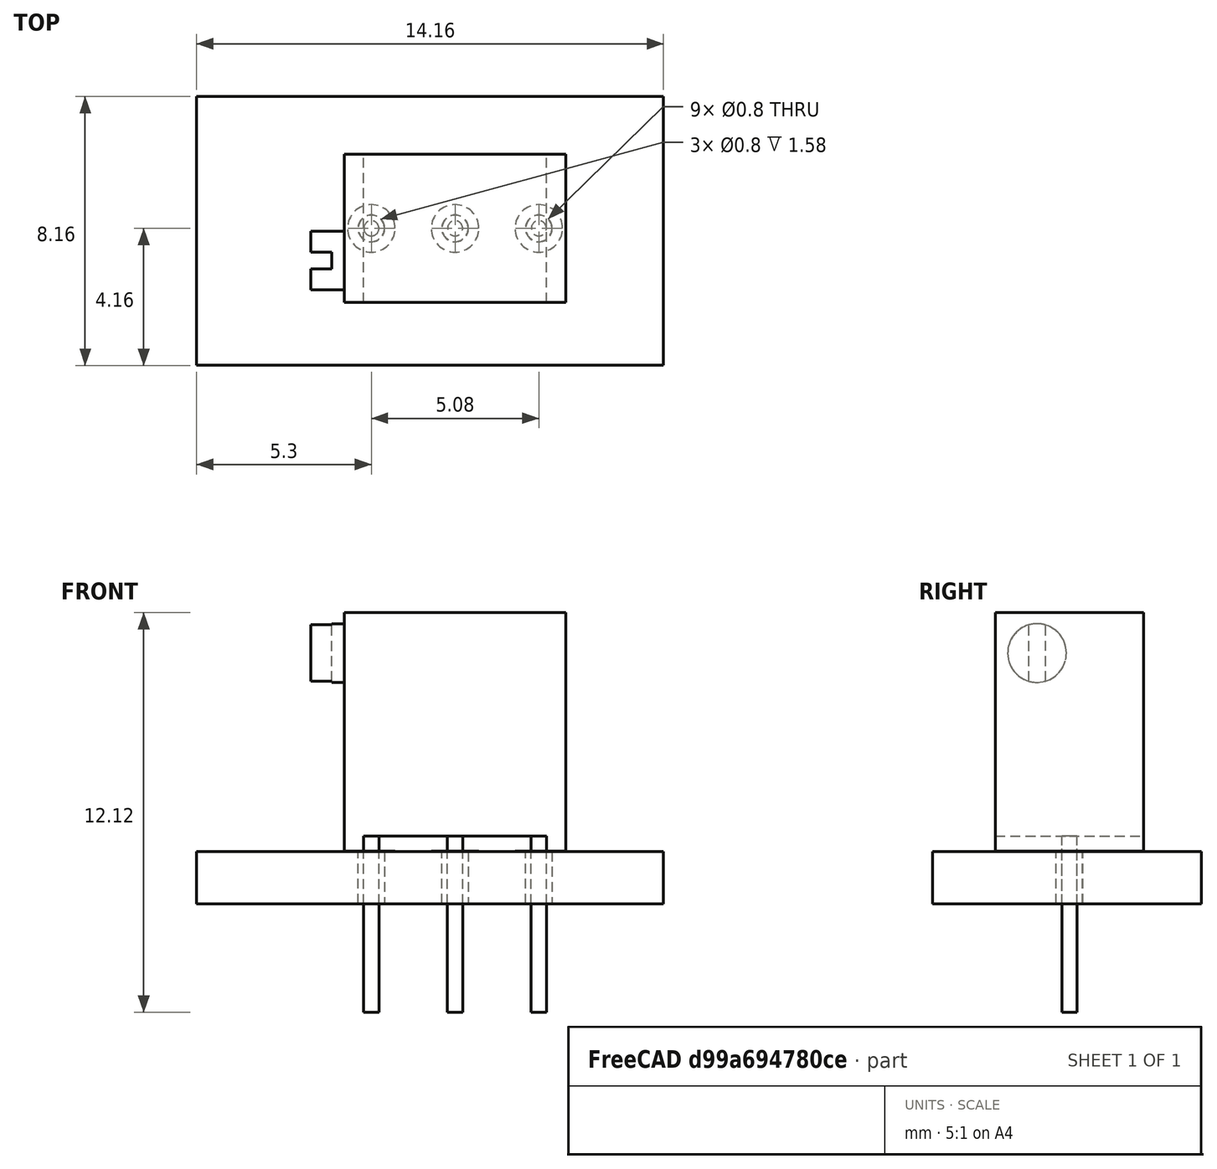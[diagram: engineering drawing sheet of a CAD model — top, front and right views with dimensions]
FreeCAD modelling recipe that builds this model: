
FCSTD DOCUMENT  (FreeCAD 0.18R15611 (Git))
Label: Potentiometer_Bourns_3266Z_Horizontal
License: All rights reserved
LicenseURL: http://en.wikipedia.org/wiki/All_rights_reserved
objects: Part::FeaturePython×7, Part::Cylinder×4, Part::Box×4, Part::MultiFuse×2, App::DocumentObjectGroup×1, Part::Cut×1, Part::Feature×1
note: 19 computed .brp shape members not serialized (recipe doc carries the construction recipe); baked Part::Feature solids carry a one-line shape summary decoded from their .brp

FEATURE [Part::FeaturePython] FCrtYd_lines  label="FCrtYd"  # a2plus imported part (geometry in sourceFile) (typed FeaturePython)
  fixedPosition = true
FEATURE [Part::FeaturePython] FFab_lines  label="FFab"  # a2plus imported part (geometry in sourceFile) (typed FeaturePython)
  fixedPosition = true
FEATURE [Part::FeaturePython] Filk_lines  label="FrontSilk"  # a2plus imported part (geometry in sourceFile) (typed FeaturePython)
  fixedPosition = true
FEATURE [Part::FeaturePython] TopPads  # a2plus imported part (geometry in sourceFile) (typed FeaturePython)
  fixedPosition = true
FEATURE [Part::FeaturePython] BotPads  # a2plus imported part (geometry in sourceFile) (typed FeaturePython)
  fixedPosition = true
FEATURE [Part::FeaturePython] THPs  label="PTHs"  # a2plus imported part (geometry in sourceFile) (typed FeaturePython)
  fixedPosition = true
FEATURE [Part::FeaturePython] newPCB  label="Pcb"  # a2plus imported part (geometry in sourceFile) (typed FeaturePython)
  fixedPosition = true
FEATURE [App::DocumentObjectGroup] Potentiometer_Bourns_3266Z_Horizontal_fp
  Group = -> [FCrtYd_lines,FFab_lines,Filk_lines,TopPads,BotPads,THPs,newPCB]
FEATURE [Part::Cylinder] Cylinder003  label="Knob"
  Angle = 360
  AttacherType = Attacher::AttachEngine3D
  Height = 1.02
  Placement = pos=(-0.405,-2.25,7.24) rot=(0,0,1;0rad)
  Radius = 0.89
FEATURE [Part::Cylinder] Cylinder001  label="Pin3"
  Angle = 360
  AttacherType = Attacher::AttachEngine3D
  Height = 5.34
  Placement = pos=(-5.08,0,-4.88) rot=(0,0,1;0rad)
  Radius = 0.23
FEATURE [Part::Box] Box003  label="Cube"
  AttacherType = Attacher::AttachEngine3D
  Height = 0.64
  Length = 10
  Placement = pos=(-5,-2.5,7.62) rot=(0,0,1;0rad)
  Width = 0.51
FEATURE [Part::Cylinder] Cylinder002  label="Pin2"
  Angle = 360
  AttacherType = Attacher::AttachEngine3D
  Height = 5.34
  Placement = pos=(-2.54,0,-4.88) rot=(0,0,1;0rad)
  Radius = 0.23
FEATURE [Part::Cylinder] Cylinder  label="Pin1"
  Angle = 360
  AttacherType = Attacher::AttachEngine3D
  Height = 5.34
  Placement = pos=(0,0,-4.88) rot=(0,0,1;0rad)
  Radius = 0.23
FEATURE [Part::Box] Box  label="Body"
  AttacherType = Attacher::AttachEngine3D
  Height = 6.78
  Length = 6.71
  Placement = pos=(-5.895,-3.52,0.46) rot=(0,0,1;0rad)
  Width = 4.5
FEATURE [Part::Box] Box001  label="Standoff1"
  AttacherType = Attacher::AttachEngine3D
  Height = 0.46
  Length = 0.585
  Placement = pos=(0.23,-3.52,0) rot=(0,0,1;0rad)
  Width = 4.5
FEATURE [Part::Box] Box002  label="Standoff2"
  AttacherType = Attacher::AttachEngine3D
  Height = 0.46
  Length = 0.585
  Placement = pos=(-5.895,-3.52,0) rot=(0,0,1;0rad)
  Width = 4.5
FEATURE [Part::MultiFuse] Fusion  label="FusionBody"
  Placement = pos=(0,1.27,0) rot=(0,0,1;0rad)
  Refine = true
  Shapes = -> [Box,Box001,Box002]
FEATURE [Part::Cut] Cut  label="CutKnob"
  Base = -> Cylinder003
  Placement = pos=(1.345,1.27,6.42) rot=(0,-1,0;1.5708rad)
  Refine = true
  Tool = -> Box003
FEATURE [Part::MultiFuse] Pin3_mp_cp  label="Pin3_fd"
  Refine = true
  Shapes = -> [Cylinder001,Cylinder002,Cylinder,Fusion,Cut]
FEATURE [Part::Feature] Shape  label="Potentiometer_Bourns_3266Z_Horizontal"
  shape: bbox 7.73 x 4.5 x 12.12 mm, 22 faces (baked)
